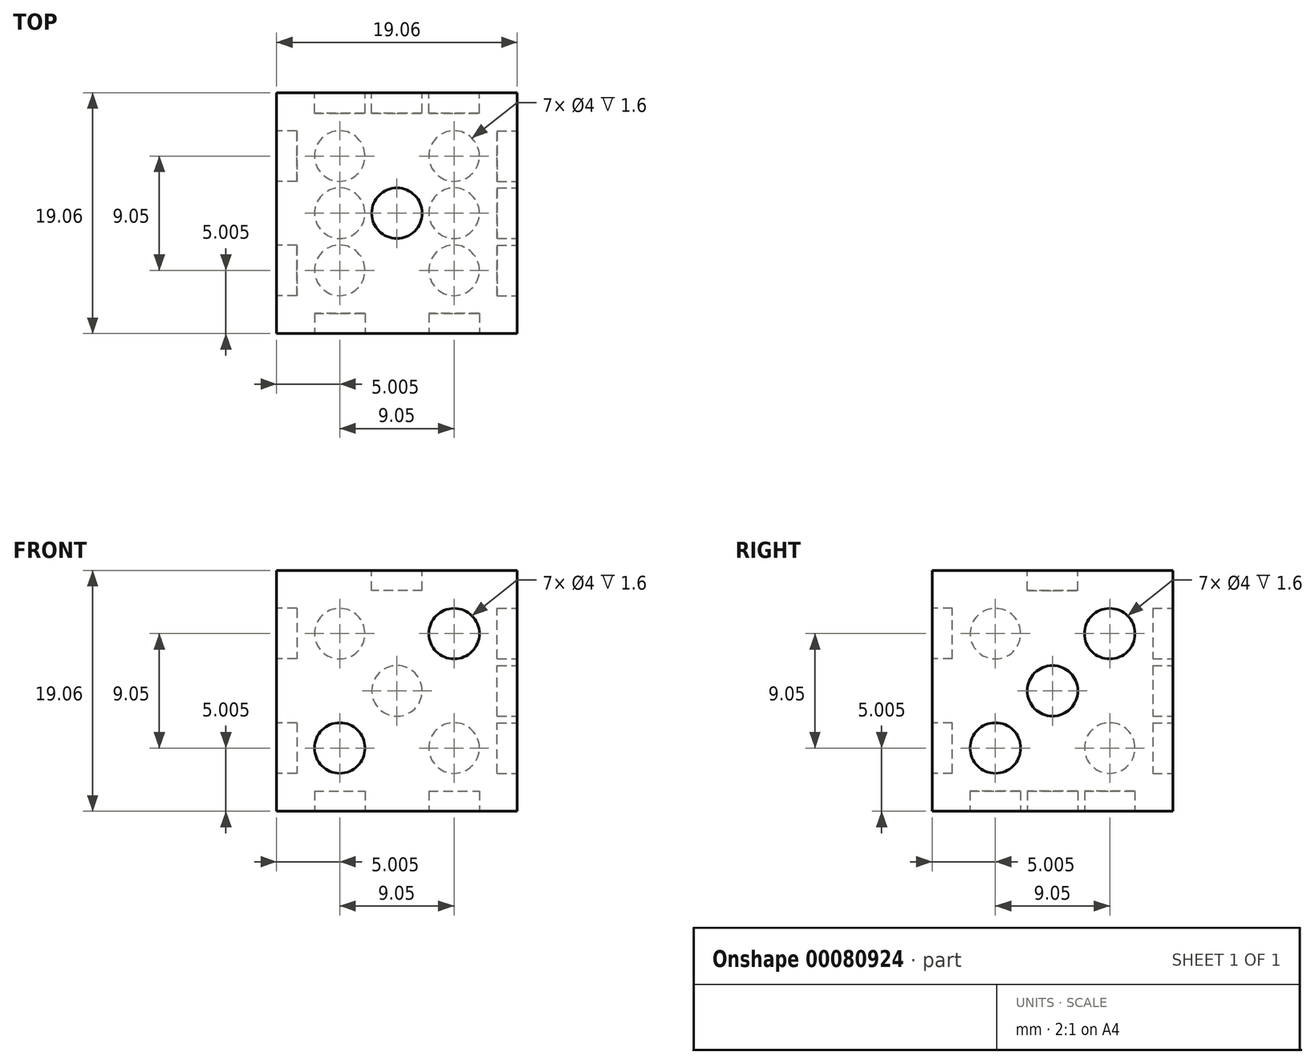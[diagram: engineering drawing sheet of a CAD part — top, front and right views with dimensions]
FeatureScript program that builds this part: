
annotation { "Feature Type Name" : "Feature", "Feature Type Description" : "" }
export const myFeature = defineFeature(function(context is Context, id is Id, definition is map)
    precondition{}
    {
        {
            var Q0;
            Q0=qCreatedBy(makeId("Top.planeOp"),FACE);
            var sketch = newSketch(context, id + "F0", { "sketchPlane" : qUnion([Q0])});
            skLineSegment(sketch, "E0.bottom", {"start": v(9.53, -9.53) * mm, "end": v(-9.53, -9.53) * mm});
            skLineSegment(sketch, "E0.top", {"start": v(9.53, 9.53) * mm, "end": v(-9.52, 9.53) * mm});
            skLineSegment(sketch, "E0.left", {"start": v(9.53, -9.53) * mm, "end": v(9.53, 9.53) * mm});
            skLineSegment(sketch, "E0.right", {"start": v(-9.53, -9.53) * mm, "end": v(-9.53, 9.52) * mm});
            skPoint(sketch, "E0.middle", {"position": v(0, 0) * mm});
            skSolve(sketch);
        }
        {
            var Q0;
            Q0 = qSketchRegion(id + "F0", true);
            extrude(context, id + "F1", {"entities" : qUnion([Q0]), "endBound" : BoundingType.SYMMETRIC, "depth" : 19.05 * mm});
        }
        {
            var Q0;
            Q0=makeQuery(id+"F1.opExtrude","CAP_FACE",FACE,{"disambiguationData":[OSD([sQuery(id+"F0.wireOp",EDGE,"E0.bottom"),sQuery(id+"F0.wireOp",EDGE,"E0.top"),sQuery(id+"F0.wireOp",EDGE,"E0.left"),sQuery(id+"F0.wireOp",EDGE,"E0.right")])],"isStart":false});
            var sketch = newSketch(context, id + "F2", { "sketchPlane" : qUnion([Q0])});
            skCircle(sketch, "E1", {"center": v(0, 0) * mm, "radius": 2 * mm});
            skSolve(sketch);
        }
        {
            var Q0;
            Q0 = qSketchRegion(id + "F2", true);
            extrude(context, id + "F3", {"entities" : qUnion([Q0]), "operationType" : NewBodyOperationType.REMOVE, "oppositeDirection" : true, "depth" : 1.6 * mm});
        }
        {
            var Q0;
            Q0=makeQuery(id+"F1.opExtrude","SWEPT_FACE",FACE,{"disambiguationData":[OSD([sQuery(id+"F0.wireOp",EDGE,"E0.bottom")])]});
            var sketch = newSketch(context, id + "F4", { "sketchPlane" : qUnion([Q0])});
            skCircle(sketch, "E2", {"center": v(-4.53, -4.52) * mm, "radius": 2 * mm});
            skCircle(sketch, "E3", {"center": v(4.52, 4.53) * mm, "radius": 2 * mm});
            skSolve(sketch);
        }
        {
            var Q0;
            Q0 = qSketchRegion(id + "F4", true);
            extrude(context, id + "F5", {"entities" : qUnion([Q0]), "operationType" : NewBodyOperationType.REMOVE, "oppositeDirection" : true, "depth" : 1.6 * mm});
        }
        {
            var Q0;
            Q0=makeQuery(id+"F1.opExtrude","CAP_FACE",FACE,{"disambiguationData":[OSD([sQuery(id+"F0.wireOp",EDGE,"E0.bottom"),sQuery(id+"F0.wireOp",EDGE,"E0.top"),sQuery(id+"F0.wireOp",EDGE,"E0.left"),sQuery(id+"F0.wireOp",EDGE,"E0.right")])],"isStart":true});
            var sketch = newSketch(context, id + "F6", { "sketchPlane" : qUnion([Q0])});
            skCircle(sketch, "E4", {"center": v(-4.53, -4.53) * mm, "radius": 2 * mm});
            skCircle(sketch, "E5.0.1.0", {"center": v(-4.53, 4.53) * mm, "radius": 2 * mm});
            skCircle(sketch, "E5.1.0.0", {"center": v(4.53, -4.53) * mm, "radius": 2 * mm});
            skCircle(sketch, "E5.1.1.0", {"center": v(4.53, 4.53) * mm, "radius": 2 * mm});
            skLineSegment(sketch, "E5.direction1", {"start": v(-4.53, -4.53) * mm, "end": v(4.53, -4.53) * mm, "construction": true});
            skLineSegment(sketch, "E5.direction2", {"start": v(-4.53, -4.53) * mm, "end": v(-4.53, 4.53) * mm, "construction": true});
            skCircle(sketch, "E6", {"center": v(-4.53, 0) * mm, "radius": 2 * mm});
            skCircle(sketch, "E7", {"center": v(4.53, 0) * mm, "radius": 2 * mm});
            skSolve(sketch);
        }
        {
            var Q0;
            Q0 = qSketchRegion(id + "F6", true);
            extrude(context, id + "F7", {"entities" : qUnion([Q0]), "operationType" : NewBodyOperationType.REMOVE, "oppositeDirection" : true, "depth" : 1.6 * mm});
        }
        {
            var Q0;
            Q0=makeQuery(id+"F1.opExtrude","SWEPT_FACE",FACE,{"disambiguationData":[OSD([sQuery(id+"F0.wireOp",EDGE,"E0.top")])]});
            var sketch = newSketch(context, id + "F8", { "sketchPlane" : qUnion([Q0])});
            skCircle(sketch, "E8", {"center": v(-4.53, -4.52) * mm, "radius": 2 * mm});
            skCircle(sketch, "E9", {"center": v(0, 0) * mm, "radius": 2 * mm});
            skCircle(sketch, "E10.0.1.0", {"center": v(-4.53, 4.53) * mm, "radius": 2 * mm});
            skCircle(sketch, "E10.1.0.0", {"center": v(4.53, -4.52) * mm, "radius": 2 * mm});
            skCircle(sketch, "E10.1.1.0", {"center": v(4.53, 4.53) * mm, "radius": 2 * mm});
            skLineSegment(sketch, "E10.direction1", {"start": v(-4.53, -4.52) * mm, "end": v(4.53, -4.52) * mm, "construction": true});
            skLineSegment(sketch, "E10.direction2", {"start": v(-4.53, -4.52) * mm, "end": v(-4.53, 4.53) * mm, "construction": true});
            skSolve(sketch);
        }
        {
            var Q0;
            Q0 = qSketchRegion(id + "F8", true);
            extrude(context, id + "F9", {"entities" : qUnion([Q0]), "operationType" : NewBodyOperationType.REMOVE, "oppositeDirection" : true, "depth" : 1.6 * mm});
        }
        {
            var Q0;
            Q0=makeQuery(id+"F1.opExtrude","SWEPT_FACE",FACE,{"disambiguationData":[OSD([sQuery(id+"F0.wireOp",EDGE,"E0.left")])]});
            var sketch = newSketch(context, id + "F10", { "sketchPlane" : qUnion([Q0])});
            skCircle(sketch, "E11", {"center": v(-4.53, -4.52) * mm, "radius": 2 * mm});
            skCircle(sketch, "E12", {"center": v(0, 0) * mm, "radius": 2 * mm});
            skCircle(sketch, "E13", {"center": v(4.53, 4.53) * mm, "radius": 2 * mm});
            skSolve(sketch);
        }
        {
            var Q0;
            Q0 = qSketchRegion(id + "F10", true);
            extrude(context, id + "F11", {"entities" : qUnion([Q0]), "operationType" : NewBodyOperationType.REMOVE, "oppositeDirection" : true, "depth" : 1.6 * mm});
        }
        {
            var Q0;
            Q0=makeQuery(id+"F1.opExtrude","SWEPT_FACE",FACE,{"disambiguationData":[OSD([sQuery(id+"F0.wireOp",EDGE,"E0.right")])]});
            var sketch = newSketch(context, id + "F12", { "sketchPlane" : qUnion([Q0])});
            skCircle(sketch, "E14", {"center": v(-4.52, -4.52) * mm, "radius": 2 * mm});
            skCircle(sketch, "E15.0.1.0", {"center": v(-4.52, 4.53) * mm, "radius": 2 * mm});
            skCircle(sketch, "E15.1.0.0", {"center": v(4.53, -4.52) * mm, "radius": 2 * mm});
            skCircle(sketch, "E15.1.1.0", {"center": v(4.53, 4.53) * mm, "radius": 2 * mm});
            skLineSegment(sketch, "E15.direction1", {"start": v(-4.52, -4.52) * mm, "end": v(4.53, -4.52) * mm, "construction": true});
            skLineSegment(sketch, "E15.direction2", {"start": v(-4.52, -4.52) * mm, "end": v(-4.52, 4.53) * mm, "construction": true});
            skSolve(sketch);
        }
        {
            var Q0;
            Q0 = qSketchRegion(id + "F12", true);
            extrude(context, id + "F13", {"entities" : qUnion([Q0]), "operationType" : NewBodyOperationType.REMOVE, "oppositeDirection" : true, "depth" : 1.6 * mm});
        }
    });
